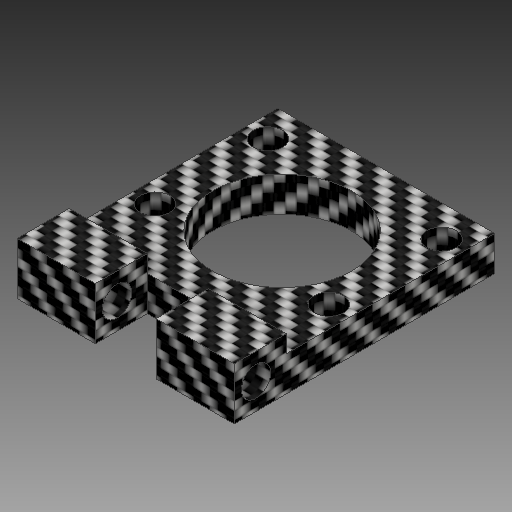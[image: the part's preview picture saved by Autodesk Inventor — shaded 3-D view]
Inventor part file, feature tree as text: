
AUTODESK INVENTOR PART (.ipt)
format: ipt  version: 2018 (Build 220112000, 112)  size: 277,504 bytes
history: native  units: mm
features: extrude x6, sketch x6, projected_geometry x1
ambient origin geometry x8: Origin, YZ Plane, XZ Plane, XY Plane, X Axis, Y Axis, Z Axis, Center Point
bodies: Volumenkörper1 (feature_tree)
feature tree (13):
  extrude  "Extrusion1"  Depth=25.0mm
  extrude  "Extrusion2"  Depth=16.0mm
  extrude  "Extrusion4"  Depth=18.0mm
  extrude  "Extrusion5"  Depth=10.0mm
  extrude  "Extrusion6"  Depth=2.5mm
  extrude  "Extrusion7"  Depth=2.0mm
  sketch  "Skizze1"  dims[d0=30.0mm d1=25.0mm]
  sketch  "Skizze2"  dims[d2=6.0mm d3=0.0mm d4=16.0mm]
  sketch  "Skizze4"  dims[d5=12.5mm d6=18.0mm]
  sketch  "Skizze6"  dims[d7=10.0mm d8=0.0mm d12=20.0mm]
  sketch  "Skizze7"  dims[d13=13.0mm d14=2.5mm]
  sketch  "Skizze8"  dims[d15=3.4mm d16=3.4mm d17=3.4mm d18=3.4mm d19=10.0mm d20=0.0mm d21=9.0mm d22=9.0mm d23=6.0mm d24=10.0mm d25=0.0mm d26=3.4mm d27=3.0mm d28=2.5mm d29=40.0mm d30=0.0mm d31=2.0mm d32=0.0mm]
  projected_geometry  "Projizierte Kontur1"
